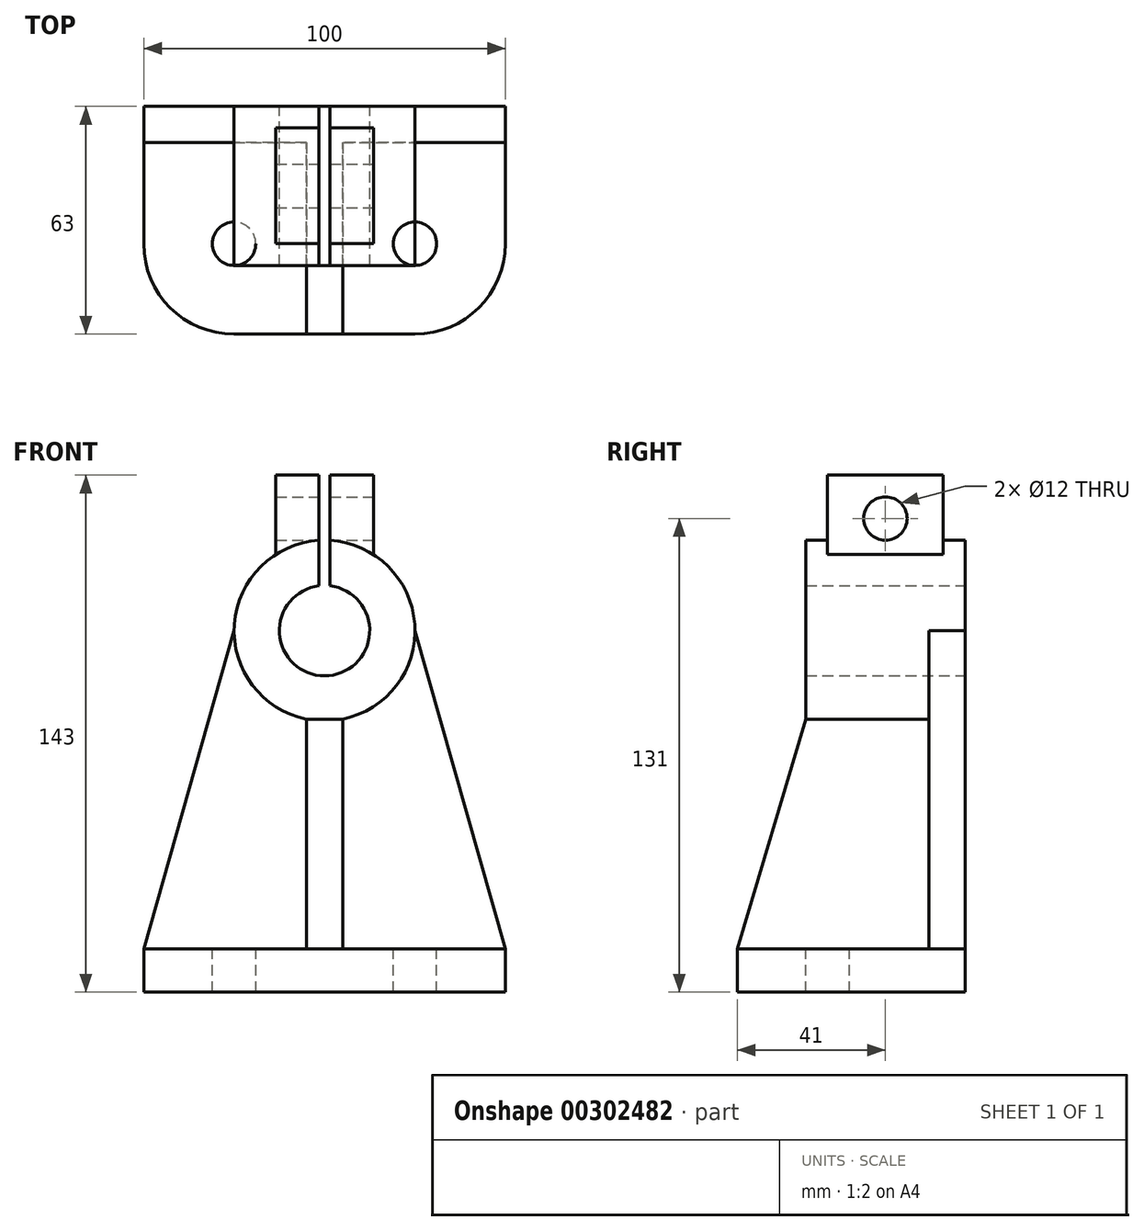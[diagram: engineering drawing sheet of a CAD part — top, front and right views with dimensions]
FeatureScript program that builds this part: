
annotation { "Feature Type Name" : "Feature", "Feature Type Description" : "" }
export const myFeature = defineFeature(function(context is Context, id is Id, definition is map)
    precondition{}
    {
        {
            var Q0;
            Q0=qCreatedBy(makeId("Top.planeOp"),FACE);
            var sketch = newSketch(context, id + "F0", { "sketchPlane" : qUnion([Q0])});
            skLineSegment(sketch, "E0.bottom", {"start": v(50, -31.5) * mm, "end": v(-50, -31.5) * mm});
            skLineSegment(sketch, "E0.top", {"start": v(50, 31.5) * mm, "end": v(-50, 31.5) * mm});
            skLineSegment(sketch, "E0.left", {"start": v(50, -31.5) * mm, "end": v(50, 31.5) * mm});
            skLineSegment(sketch, "E0.right", {"start": v(-50, -31.5) * mm, "end": v(-50, 31.5) * mm});
            skPoint(sketch, "E0.middle", {"position": v(0, 0) * mm});
            skSolve(sketch);
        }
        {
            var Q0;
            Q0=makeQuery(id+"F0.imprint","IMPRINT",FACE,{"disambiguationData":[TD([[makeQuery(id+"F0.imprint","IMPRINT",EDGE,{"derivedFrom":sQuery(id+"F0.wireOp",EDGE,"E0.bottom")}),-1.0]])]});
            extrude(context, id + "F1", {"entities" : qUnion([Q0]), "depth" : 12 * mm});
        }
        {
            var Q0;
            Q0=makeQuery(id+"F1.opExtrude","SWEPT_EDGE",EDGE,{"disambiguationData":[OSD([sQuery(id+"F0.wireOp",EDGE,"E0.bottom"),sQuery(id+"F0.wireOp",EDGE,"E0.right")])]});
            var Q1;
            Q1=makeQuery(id+"F1.opExtrude","SWEPT_EDGE",EDGE,{"disambiguationData":[OSD([sQuery(id+"F0.wireOp",EDGE,"E0.bottom"),sQuery(id+"F0.wireOp",EDGE,"E0.left")])]});
            fillet(context, id + "F2", {"entities" : qUnion([Q0, Q1]), "radius" : 25 * mm, "tangentPropagation" : true, "allowEdgeOverflow" : false});
        }
        {
            var Q0;
            Q0=makeQuery(id+"F1.opExtrude","CAP_FACE",FACE,{"disambiguationData":[OSD([sQuery(id+"F0.wireOp",EDGE,"E0.bottom"),sQuery(id+"F0.wireOp",EDGE,"E0.top"),sQuery(id+"F0.wireOp",EDGE,"E0.left"),sQuery(id+"F0.wireOp",EDGE,"E0.right")])],"isStart":false});
            var sketch = newSketch(context, id + "F3", { "sketchPlane" : qUnion([Q0])});
            skCircle(sketch, "E1", {"center": v(-25, -6.5) * mm, "radius": 6 * mm});
            skSolve(sketch);
        }
        {
            var Q0;
            Q0=makeQuery(id+"F3.imprint","IMPRINT",FACE,{"disambiguationData":[TD([[makeQuery(id+"F3.imprint","IMPRINT",EDGE,{"derivedFrom":sQuery(id+"F3.wireOp",EDGE,"E1")}),1.0]])]});
            var Q1;
            Q1=sQuery(id+"F3.wireOp",EDGE,"E1");
            extrude(context, id + "F4", {"entities" : qUnion([Q0]), "operationType" : NewBodyOperationType.REMOVE, "surfaceEntities" : qUnion([Q1]), "endBound" : BoundingType.UP_TO_NEXT, "oppositeDirection" : true, "depth" : 25 * mm});
        }
        {
            var Q0;
            Q0=makeQuery(id+"F1.opExtrude","CAP_FACE",FACE,{"disambiguationData":[OSD([sQuery(id+"F0.wireOp",EDGE,"E0.bottom"),sQuery(id+"F0.wireOp",EDGE,"E0.top"),sQuery(id+"F0.wireOp",EDGE,"E0.left"),sQuery(id+"F0.wireOp",EDGE,"E0.right")])],"isStart":false});
            var sketch = newSketch(context, id + "F5", { "sketchPlane" : qUnion([Q0])});
            skCircle(sketch, "E2", {"center": v(25, -6.5) * mm, "radius": 6 * mm});
            skSolve(sketch);
        }
        {
            var Q0;
            Q0=makeQuery(id+"F5.imprint","IMPRINT",FACE,{"disambiguationData":[TD([[makeQuery(id+"F5.imprint","IMPRINT",EDGE,{"derivedFrom":sQuery(id+"F5.wireOp",EDGE,"E2")}),1.0]])]});
            var Q1;
            Q1=sQuery(id+"F5.wireOp",EDGE,"E2");
            extrude(context, id + "F6", {"entities" : qUnion([Q0]), "operationType" : NewBodyOperationType.REMOVE, "surfaceEntities" : qUnion([Q1]), "endBound" : BoundingType.UP_TO_NEXT, "oppositeDirection" : true, "depth" : 25 * mm});
        }
        {
            var Q0;
            Q0=makeQuery(id+"F1.opExtrude","SWEPT_FACE",FACE,{"disambiguationData":[OSD([sQuery(id+"F0.wireOp",EDGE,"E0.top")])]});
            var sketch = newSketch(context, id + "F7", { "sketchPlane" : qUnion([Q0])});
            skCircle(sketch, "E3", {"center": v(0, 100) * mm, "radius": 25 * mm});
            skCircle(sketch, "E4", {"center": v(0, 100) * mm, "radius": 12.5 * mm});
            skSolve(sketch);
        }
        {
            var Q0;
            Q0=makeQuery(id+"F7.imprint","IMPRINT",FACE,{"disambiguationData":[TD([[makeQuery(id+"F7.imprint","IMPRINT",EDGE,{"derivedFrom":sQuery(id+"F7.wireOp",EDGE,"E3")}),1.0]])]});
            var Q1;
            Q1=sQuery(id+"F7.wireOp",EDGE,"E3");
            extrude(context, id + "F8", {"entities" : qUnion([Q0]), "surfaceEntities" : qUnion([Q1]), "oppositeDirection" : true, "depth" : 44 * mm});
        }
        {
            var Q0;
            Q0=makeQuery(id+"F1.opExtrude","CAP_FACE",FACE,{"disambiguationData":[OSD([sQuery(id+"F0.wireOp",EDGE,"E0.bottom"),sQuery(id+"F0.wireOp",EDGE,"E0.top"),sQuery(id+"F0.wireOp",EDGE,"E0.left"),sQuery(id+"F0.wireOp",EDGE,"E0.right")])],"isStart":false});
            var sketch = newSketch(context, id + "F9", { "sketchPlane" : qUnion([Q0])});
            skLineSegment(sketch, "E5.bottom", {"start": v(25, 21.5) * mm, "end": v(-25, 21.5) * mm});
            skLineSegment(sketch, "E5.top", {"start": v(25, 31.5) * mm, "end": v(-25, 31.5) * mm});
            skLineSegment(sketch, "E5.left", {"start": v(25, 21.5) * mm, "end": v(25, 31.5) * mm});
            skLineSegment(sketch, "E5.right", {"start": v(-25, 21.5) * mm, "end": v(-25, 31.5) * mm});
            skPoint(sketch, "E5.middle", {"position": v(0, 26.5) * mm});
            skSolve(sketch);
        }
        {
            var Q0;
            Q0=makeQuery(id+"F9.imprint","IMPRINT",FACE,{"disambiguationData":[TD([[makeQuery(id+"F9.imprint","IMPRINT",EDGE,{"derivedFrom":sQuery(id+"F9.wireOp",EDGE,"E5.bottom")}),-1.0]])]});
            extrude(context, id + "F10", {"entities" : qUnion([Q0]), "operationType" : NewBodyOperationType.ADD, "endBound" : BoundingType.UP_TO_NEXT, "depth" : 25 * mm});
        }
        {
            var Q0;
            Q0=makeQuery(id+"F10.boolean.opBoolean","MERGE",FACE,{"derivedFrom":[makeQuery(id+"F1.opExtrude","SWEPT_FACE",FACE,{"disambiguationData":[OSD([sQuery(id+"F0.wireOp",EDGE,"E0.top")])]}),makeQuery(id+"F8.opExtrude","CAP_FACE",FACE,{"disambiguationData":[OSD([sQuery(id+"F7.wireOp",EDGE,"E3"),sQuery(id+"F7.wireOp",EDGE,"E4")])],"isStart":true}),makeQuery(id+"F10.opExtrude","SWEPT_FACE",FACE,{"disambiguationData":[OSD([sQuery(id+"F9.wireOp",EDGE,"E5.top")])]})]});
            var sketch = newSketch(context, id + "F11", { "sketchPlane" : qUnion([Q0])});
            skLineSegment(sketch, "E6", {"start": v(-50, 12) * mm, "end": v(-25, 12) * mm});
            skLineSegment(sketch, "E7", {"start": v(-25, 100) * mm, "end": v(-25, 12) * mm});
            skLineSegment(sketch, "E8", {"start": v(-25, 100) * mm, "end": v(-50, 12) * mm});
            skSolve(sketch);
        }
        {
            var Q0;
            Q0=makeQuery(id+"F11.imprint","IMPRINT",FACE,{"disambiguationData":[TD([[makeQuery(id+"F11.imprint","IMPRINT",EDGE,{"derivedFrom":sQuery(id+"F11.wireOp",EDGE,"E6")}),1.0]])]});
            extrude(context, id + "F12", {"entities" : qUnion([Q0]), "operationType" : NewBodyOperationType.ADD, "oppositeDirection" : true, "depth" : 10 * mm});
        }
        {
            var Q0;
            Q0=makeQuery(id+"F12.boolean.opBoolean","MERGE",FACE,{"derivedFrom":[makeQuery(id+"F10.boolean.opBoolean","MERGE",FACE,{"derivedFrom":[makeQuery(id+"F1.opExtrude","SWEPT_FACE",FACE,{"disambiguationData":[OSD([sQuery(id+"F0.wireOp",EDGE,"E0.top")])]}),makeQuery(id+"F8.opExtrude","CAP_FACE",FACE,{"disambiguationData":[OSD([sQuery(id+"F7.wireOp",EDGE,"E3"),sQuery(id+"F7.wireOp",EDGE,"E4")])],"isStart":true}),makeQuery(id+"F10.opExtrude","SWEPT_FACE",FACE,{"disambiguationData":[OSD([sQuery(id+"F9.wireOp",EDGE,"E5.top")])]})]}),makeQuery(id+"F12.opExtrude","CAP_FACE",FACE,{"disambiguationData":[OSD([sQuery(id+"F11.wireOp",EDGE,"E6"),sQuery(id+"F11.wireOp",EDGE,"E7"),sQuery(id+"F11.wireOp",EDGE,"E8")])],"isStart":true})]});
            var sketch = newSketch(context, id + "F13", { "sketchPlane" : qUnion([Q0])});
            skLineSegment(sketch, "E9", {"start": v(25, 12) * mm, "end": v(50, 12) * mm});
            skLineSegment(sketch, "E10", {"start": v(50, 12) * mm, "end": v(25, 100) * mm});
            skLineSegment(sketch, "E11", {"start": v(25, 100) * mm, "end": v(25, 12) * mm});
            skSolve(sketch);
        }
        {
            var Q0;
            Q0=makeQuery(id+"F13.imprint","IMPRINT",FACE,{"disambiguationData":[TD([[makeQuery(id+"F13.imprint","IMPRINT",EDGE,{"derivedFrom":sQuery(id+"F13.wireOp",EDGE,"E9")}),1.0]])]});
            extrude(context, id + "F14", {"entities" : qUnion([Q0]), "operationType" : NewBodyOperationType.ADD, "oppositeDirection" : true, "depth" : 10 * mm});
        }
        {
            var Q0;
            Q0=qCreatedBy(makeId("Top.planeOp"),FACE);
            cPlane(context, id + "F15", {"entities" : qUnion([Q0]), "cplaneType" : CPlaneType.OFFSET, "offset" : 120 * mm, "width" : 150 * mm, "height" : 150 * mm});
        }
        {
            var Q0;
            Q0=qCreatedBy(id+"F15.planeOp",FACE);
            var sketch = newSketch(context, id + "F16", { "sketchPlane" : qUnion([Q0])});
            skLineSegment(sketch, "E12.bottom", {"start": v(13.5, 25.5) * mm, "end": v(-13.5, 25.5) * mm});
            skLineSegment(sketch, "E12.top", {"start": v(13.5, -6.5) * mm, "end": v(-13.5, -6.5) * mm});
            skLineSegment(sketch, "E12.left", {"start": v(13.5, 25.5) * mm, "end": v(13.5, -6.5) * mm});
            skLineSegment(sketch, "E12.right", {"start": v(-13.5, 25.5) * mm, "end": v(-13.5, -6.5) * mm});
            skSolve(sketch);
        }
        {
            var Q0;
            Q0 = qSketchRegion(id + "F16", true);
            extrude(context, id + "F17", {"entities" : qUnion([Q0]), "operationType" : NewBodyOperationType.ADD, "depth" : 23 * mm});
        }
        {
            var Q0;
            Q0=makeQuery(id+"F1.opExtrude","CAP_FACE",FACE,{"disambiguationData":[OSD([sQuery(id+"F0.wireOp",EDGE,"E0.bottom"),sQuery(id+"F0.wireOp",EDGE,"E0.top"),sQuery(id+"F0.wireOp",EDGE,"E0.left"),sQuery(id+"F0.wireOp",EDGE,"E0.right")])],"isStart":false});
            var sketch = newSketch(context, id + "F18", { "sketchPlane" : qUnion([Q0])});
            skLineSegment(sketch, "E13.bottom", {"start": v(5, 21.5) * mm, "end": v(-5, 21.5) * mm});
            skLineSegment(sketch, "E13.top", {"start": v(5, -12.5) * mm, "end": v(-5, -12.5) * mm});
            skLineSegment(sketch, "E13.left", {"start": v(5, 21.5) * mm, "end": v(5, -12.5) * mm});
            skLineSegment(sketch, "E13.right", {"start": v(-5, 21.5) * mm, "end": v(-5, -12.5) * mm});
            skPoint(sketch, "E13.middle", {"position": v(0, 4.5) * mm});
            skSolve(sketch);
        }
        {
            var Q0;
            Q0=makeQuery(id+"F18.imprint","IMPRINT",FACE,{"disambiguationData":[TD([[makeQuery(id+"F18.imprint","IMPRINT",EDGE,{"derivedFrom":sQuery(id+"F18.wireOp",EDGE,"E13.bottom")}),1.0]])]});
            extrude(context, id + "F19", {"entities" : qUnion([Q0]), "operationType" : NewBodyOperationType.ADD, "endBound" : BoundingType.UP_TO_NEXT, "depth" : 25 * mm});
        }
        {
            var Q0;
            Q0=makeQuery(id+"F19.opExtrude","SWEPT_FACE",FACE,{"disambiguationData":[OSD([sQuery(id+"F18.wireOp",EDGE,"E13.right")])]});
            var sketch = newSketch(context, id + "F20", { "sketchPlane" : qUnion([Q0])});
            skLineSegment(sketch, "E14", {"start": v(12.5, 75.5) * mm, "end": v(12.5, 12) * mm});
            skLineSegment(sketch, "E15", {"start": v(12.5, 12) * mm, "end": v(31.42, 12) * mm});
            skLineSegment(sketch, "E16", {"start": v(31.42, 12) * mm, "end": v(12.5, 75.5) * mm});
            skSolve(sketch);
        }
        {
            var Q0;
            Q0=makeQuery(id+"F20.imprint","IMPRINT",FACE,{"disambiguationData":[TD([[makeQuery(id+"F20.imprint","IMPRINT",EDGE,{"derivedFrom":sQuery(id+"F20.wireOp",EDGE,"E14")}),1.0]])]});
            extrude(context, id + "F21", {"entities" : qUnion([Q0]), "operationType" : NewBodyOperationType.ADD, "oppositeDirection" : true, "depth" : 10 * mm});
        }
        {
            var Q0;
            Q0=qCreatedBy(id+"F15.planeOp",FACE);
            var sketch = newSketch(context, id + "F22", { "sketchPlane" : qUnion([Q0])});
            skLineSegment(sketch, "E17.bottom", {"start": v(-1.5, 33.33) * mm, "end": v(1.5, 33.33) * mm});
            skLineSegment(sketch, "E17.top", {"start": v(-1.5, -26.67) * mm, "end": v(1.5, -26.67) * mm});
            skLineSegment(sketch, "E17.left", {"start": v(-1.5, 33.33) * mm, "end": v(-1.5, -26.67) * mm});
            skLineSegment(sketch, "E17.right", {"start": v(1.5, 33.33) * mm, "end": v(1.5, -26.67) * mm});
            skPoint(sketch, "E17.middle", {"position": v(0, 3.33) * mm});
            skSolve(sketch);
        }
        {
            var Q0;
            Q0=makeQuery(id+"F22.imprint","IMPRINT",FACE,{"disambiguationData":[TD([[makeQuery(id+"F22.imprint","IMPRINT",EDGE,{"derivedFrom":sQuery(id+"F22.wireOp",EDGE,"E17.bottom")}),-1.0]])]});
            extrude(context, id + "F23", {"entities" : qUnion([Q0]), "operationType" : NewBodyOperationType.REMOVE, "oppositeDirection" : true, "depth" : 25 * mm, "hasSecondDirection" : true, "secondDirectionOppositeDirection" : false, "secondDirectionDepth" : 25 * mm});
        }
        {
            var Q0;
            Q0=makeQuery(id+"F17.opExtrude","SWEPT_FACE",FACE,{"disambiguationData":[OSD([sQuery(id+"F16.wireOp",EDGE,"E12.left")])]});
            var sketch = newSketch(context, id + "F24", { "sketchPlane" : qUnion([Q0])});
            skCircle(sketch, "E18", {"center": v(9.5, 131) * mm, "radius": 6 * mm});
            skSolve(sketch);
        }
        {
            var Q0;
            Q0=makeQuery(id+"F24.imprint","IMPRINT",FACE,{"disambiguationData":[TD([[makeQuery(id+"F24.imprint","IMPRINT",EDGE,{"derivedFrom":sQuery(id+"F24.wireOp",EDGE,"E18")}),1.0]])]});
            extrude(context, id + "F25", {"entities" : qUnion([Q0]), "operationType" : NewBodyOperationType.REMOVE, "endBound" : BoundingType.THROUGH_ALL, "oppositeDirection" : true, "depth" : 25 * mm});
        }
    });
